# Revit family: QF_MACOM_BMx-xxx
name_source: partatom
category: Equipamento especial
units: mm (PartAtom-declared; Revit-internal decimal feet)

## family parameters
Com base no plano de trabalho = Não
Compartilhado = Não
Corte com vazios quando carregada = Não
Cota do conector redondo = Utilizar diâmetro
Número OmniClass = 23.40.40.14.17.11
Ponto de cálculo do ambiente = Não
Sempre na vertical = Sim
Tipo de parte = Normal
Título OmniClass = Cookers, Ovens, Stoves

## types (12) — shared parameters
Cold Water Size = 1"
Cycle = 60 Hz
Elevação padrão = 0,000 mm
Fabricante = MACOM
Indirect Waste Size = 1"
Show Logo = Sim
URL = https://www.acosmacom.com.br
Volts = 220 V
Weight = 0 kg
Width = 590,000 mm
Work Temperature = 20°C - 95°C

## per-type parameters (varying)
| type | C1 | C2 | C3 | C4 | C5 | C6 | Descrição | Electric Power | GN Capacity 1/1 | Height | Length | Volume |
| BM7-160 | 93,000 mm | 546,250 mm | 998,750 mm | 1451,250 mm | 1904,500 mm | 97,875 mm | BANHO-MARIA ELETRICO PLUG-IN MACOM CAPACIDADE 07 GN´S 1/1-150, COM 5 DIVISOR DGN530 | 8000 W | 07 | 493,000 mm | 2340,000 mm | 0,70 m³ |
| BM7-210 | 93,000 mm | 546,250 mm | 998,750 mm | 1451,250 mm | 1904,500 mm | 97,875 mm | BANHO-MARIA ELETRICO PLUG-IN MACOM CAPACIDADE 07 GN´S 1/1-200 | 8000 W | 07 | 543,000 mm | 2340,000 mm | 0,70 m³ |
| BM6-160 | 93,000 mm | 546,250 mm | 998,750 mm | 1451,250 mm | 1451,250 mm | 97,875 mm | BANHO-MARIA ELETRICO PLUG-IN MACOM CAPACIDADE 06 GN´S 1/1-150, COM 5 DIVISOR DGN530 | 6400 W | 06 | 493,000 mm | 2015,000 mm | 0,60 m³ |
| BM5-160 | 119,000 mm | 492,400 mm | 865,400 mm | 1238,000 mm | 1238,000 mm | 123,880 mm | BANHO-MARIA ELETRICO PLUG-IN MACOM CAPACIDADE 05 GN´S 1/1-150, COM 4 DIVISOR DGN530 | 6400 W | 05 | 493,000 mm | 1690,000 mm | 0,50 m³ |
| BM4-160 | 119,000 mm | 508,000 mm | 897,000 mm | 897,000 mm | 897,000 mm | 123,880 mm | BANHO-MARIA ELETRICO PLUG-IN MACOM CAPACIDADE 04 GN´S 1/1-150, COM 3 DIVISOR DGN530 | 4800 W | 04 | 493,000 mm | 1365,000 mm | 0,40 m³ |
| BM3-160 | 3,510 mm | 324,500 mm | 645,500 mm | 645,500 mm | 645,500 mm | 123,880 mm | BANHO-MARIA ELETRICO PLUG-IN MACOM CAPACIDADE 03 GN´S 1/1-150, COM 2 DIVISOR DGN530 | 4800 W | 03 | 493,000 mm | 1040,000 mm | 0,30 m³ |
| BM2-160 | 3,510 mm | 320,500 mm | 320,500 mm | 320,500 mm | 320,500 mm | 123,880 mm | BANHO-MARIA ELETRICO PLUG-IN MACOM CAPACIDADE 02 GN´S 1/1-150, COM 01 DIVISOR DGN530 | 3200 W | 02 | 493,000 mm | 715,000 mm | 0,20 m³ |
| BM2-210 | 3,510 mm | 320,500 mm | 320,500 mm | 320,500 mm | 320,500 mm | 123,880 mm | BANHO-MARIA ELETRICO PLUG-IN MACOM CAPACIDADE 02 GN´S 1/1-200, COM 01 DIVISOR DGN530 | 3200 W | 02 | 543,000 mm | 715,000 mm | 0,20 m³ |
| BM3-210 | 3,510 mm | 324,500 mm | 645,500 mm | 645,500 mm | 645,500 mm | 123,880 mm | BANHO-MARIA ELETRICO PLUG-IN MACOM CAPACIDADE 03 GN´S 1/1-200, COM 2 DIVISOR DGN530 | 4800 W | 03 | 543,000 mm | 1040,000 mm | 0,30 m³ |
| BM4-210 | 119,000 mm | 508,000 mm | 897,000 mm | 897,000 mm | 897,000 mm | 123,880 mm | BANHO-MARIA ELETRICO PLUG-IN MACOM CAPACIDADE 04 GN´S 1/1-200 | 4800 W | 04 | 543,000 mm | 1365,000 mm | 0,40 m³ |
| BM5-210 | 119,000 mm | 492,400 mm | 865,400 mm | 1238,000 mm | 1238,000 mm | 123,880 mm | BANHO-MARIA ELETRICO PLUG-IN MACOM CAPACIDADE 05 GN´S 1/1-200, COM 4 DIVISOR DGN530 | 6400 W | 05 | 543,000 mm | 1690,000 mm | 0,50 m³ |
| BM6-210 | 93,000 mm | 546,250 mm | 998,750 mm | 1451,250 mm | 1451,250 mm | 97,875 mm | BANHO-MARIA ELETRICO PLUG-IN MACOM CAPACIDADE 06 GN´S 1/1-200 | 6400 W | 06 | 543,000 mm | 2015,000 mm | 0,60 m³ |

note: column(s) folded — value = type name in every type: Modelo

## geometry (parser evidence)
native form markers: Sweep x5
no freeform markers — native parametric forms only
